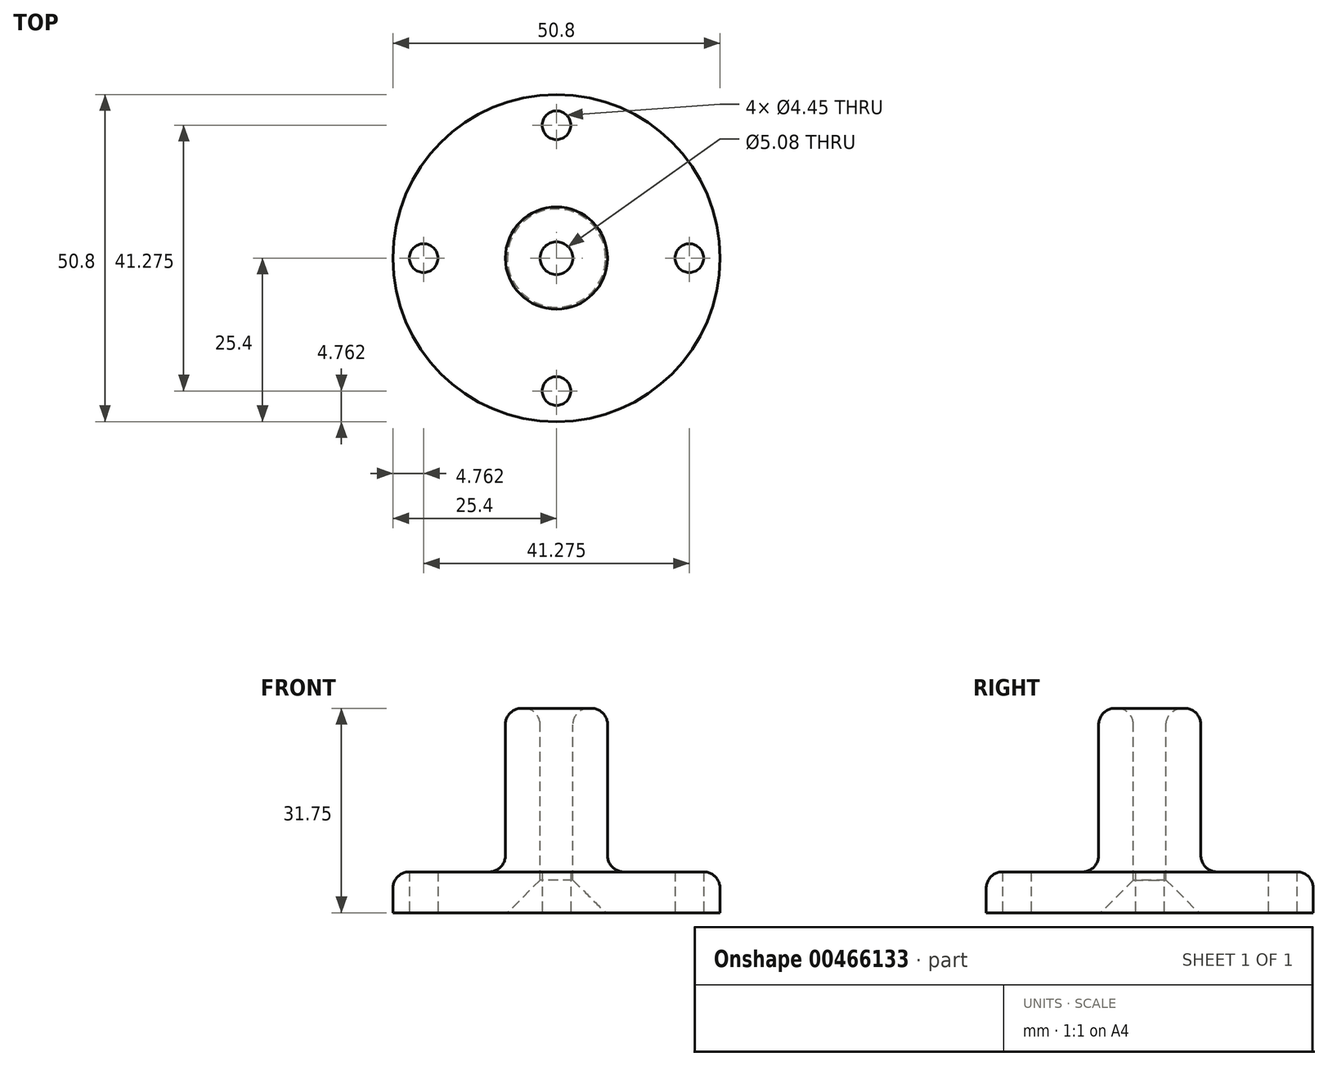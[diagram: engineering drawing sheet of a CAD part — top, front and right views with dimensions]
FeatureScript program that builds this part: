
annotation { "Feature Type Name" : "Feature", "Feature Type Description" : "" }
export const myFeature = defineFeature(function(context is Context, id is Id, definition is map)
    precondition{}
    {
        {
            var Q0;
            Q0=qCreatedBy(makeId("Top.planeOp"),FACE);
            var sketch = newSketch(context, id + "F0", { "sketchPlane" : qUnion([Q0])});
            skCircle(sketch, "E0", {"center": v(0, 0) * mm, "radius": 25.4 * mm});
            skLineSegment(sketch, "E1", {"start": v(0, 41.42) * mm, "end": v(0, -53.18) * mm, "construction": true});
            skLineSegment(sketch, "E2", {"start": v(45.55, 0) * mm, "end": v(-36.4, 0) * mm, "construction": true});
            skCircle(sketch, "E3", {"center": v(0, 0) * mm, "radius": 20.64 * mm, "construction": true});
            skCircle(sketch, "E4", {"center": v(0, 20.64) * mm, "radius": 2.22 * mm});
            skCircle(sketch, "E5.1.0", {"center": v(20.64, 0) * mm, "radius": 2.22 * mm});
            skCircle(sketch, "E5.2.0", {"center": v(0, -20.64) * mm, "radius": 2.22 * mm});
            skCircle(sketch, "E5.3.0", {"center": v(-20.64, 0) * mm, "radius": 2.22 * mm});
            skLineSegment(sketch, "E5.anchor1", {"start": v(0, 0) * mm, "end": v(0, 20.64) * mm, "construction": true});
            skLineSegment(sketch, "E5.anchor2", {"start": v(0, 0) * mm, "end": v(-20.64, 0) * mm, "construction": true});
            skArc(sketch, "E6", {"start": v(-4.06, 0) * mm, "mid": v(0, -4.06) * mm, "end": v(4.06, 0) * mm});
            skArc(sketch, "E7.0", {"start": v(1.4, 10.32) * mm, "mid": v(0.7, 10.4) * mm, "end": v(0, 10.41) * mm});
            skLineSegment(sketch, "E8", {"start": v(0, 10.32) * mm, "end": v(46.94, 10.32) * mm, "construction": true});
            skLineSegment(sketch, "E9", {"start": v(10.41, 0) * mm, "end": v(10.41, 10.32) * mm});
            skLineSegment(sketch, "E10", {"start": v(4.06, 0) * mm, "end": v(4.06, 10.32) * mm});
            skArc(sketch, "E11", {"start": v(10.41, 10.32) * mm, "mid": v(7.24, 14.11) * mm, "end": v(4.06, 10.32) * mm});
            skArc(sketch, "E12.trimOffspring", {"start": v(-10.41, 0) * mm, "mid": v(0, -10.41) * mm, "end": v(10.41, 0) * mm});
            skLineSegment(sketch, "E13.MirrorCS", {"start": v(-4.06, 0) * mm, "end": v(-4.06, 10.32) * mm});
            skArc(sketch, "E14.MirrorCS", {"start": v(-10.41, 10.32) * mm, "mid": v(-7.24, 14.11) * mm, "end": v(-4.06, 10.32) * mm});
            skLineSegment(sketch, "E15.MirrorCS", {"start": v(-10.41, 0) * mm, "end": v(-10.41, 10.32) * mm});
            skSolve(sketch);
        }
        {
            var Q0;
            Q0=makeQuery(id+"F0.imprint","IMPRINT",FACE,{"disambiguationData":[TD([[makeQuery(id+"F0.imprint","IMPRINT",EDGE,{"derivedFrom":sQuery(id+"F0.wireOp",EDGE,"E0")}),1.0]])]});
            var Q1;
            Q1=makeQuery(id+"F0.imprint","IMPRINT",FACE,{"disambiguationData":[TD([[makeQuery(id+"F0.imprint","IMPRINT",EDGE,{"derivedFrom":sQuery(id+"F0.wireOp",EDGE,"E6")}),-1.0]])]});
            var Q2;
            Q2=makeQuery(id+"F0.imprint","IMPRINT",FACE,{"disambiguationData":[TD([[makeQuery(id+"F0.imprint","IMPRINT",EDGE,{"derivedFrom":sQuery(id+"F0.wireOp",EDGE,"E5.2.0")}),1.0]])]});
            var Q3;
            Q3=makeQuery(id+"F0.imprint","IMPRINT",FACE,{"disambiguationData":[TD([[makeQuery(id+"F0.imprint","IMPRINT",EDGE,{"derivedFrom":sQuery(id+"F0.wireOp",EDGE,"E5.3.0")}),1.0]])]});
            var Q4;
            Q4=makeQuery(id+"F0.imprint","IMPRINT",FACE,{"disambiguationData":[TD([[makeQuery(id+"F0.imprint","IMPRINT",EDGE,{"derivedFrom":sQuery(id+"F0.wireOp",EDGE,"E4")}),1.0]])]});
            var Q5;
            Q5=makeQuery(id+"F0.imprint","IMPRINT",FACE,{"disambiguationData":[TD([[makeQuery(id+"F0.imprint","IMPRINT",EDGE,{"derivedFrom":sQuery(id+"F0.wireOp",EDGE,"E5.1.0")}),1.0]])]});
            extrude(context, id + "F1", {"entities" : qUnion([Q0, Q1, Q2, Q3, Q4, Q5]), "depth" : 6.35 * mm});
        }
        {
            var Q0;
            Q0=makeQuery(id+"F1.opExtrude","CAP_FACE",FACE,{"disambiguationData":[OSD([sQuery(id+"F0.wireOp",EDGE,"E0"),sQuery(id+"F0.wireOp",EDGE,"E4"),sQuery(id+"F0.wireOp",EDGE,"E5.1.0"),sQuery(id+"F0.wireOp",EDGE,"E5.2.0"),sQuery(id+"F0.wireOp",EDGE,"E5.3.0")])],"isStart":false});
            var sketch = newSketch(context, id + "F2", { "sketchPlane" : qUnion([Q0])});
            skCircle(sketch, "E16", {"center": v(0, 0) * mm, "radius": 2.54 * mm});
            skCircle(sketch, "E17", {"center": v(0, 0) * mm, "radius": 7.94 * mm});
            skSolve(sketch);
        }
        {
            var Q0;
            Q0=makeQuery(id+"F1.opExtrude","CAP_EDGE",EDGE,{"disambiguationData":[OSD([sQuery(id+"F0.wireOp",EDGE,"E0")])],"isStart":false});
            fillet(context, id + "F3", {"entities" : qUnion([Q0]), "radius" : 2.54 * mm, "tangentPropagation" : true, "allowEdgeOverflow" : false});
        }
        {
            var Q0;
            Q0=makeQuery(id+"F2.imprint","IMPRINT",FACE,{"disambiguationData":[TD([[makeQuery(id+"F2.imprint","IMPRINT",EDGE,{"derivedFrom":sQuery(id+"F2.wireOp",EDGE,"E16")}),1.0]])]});
            extrude(context, id + "F4", {"entities" : qUnion([Q0]), "operationType" : NewBodyOperationType.REMOVE, "oppositeDirection" : true, "depth" : 25.4 * mm});
        }
        {
            var Q0;
            Q0=makeQuery(id+"F2.imprint","IMPRINT",FACE,{"disambiguationData":[TD([[makeQuery(id+"F2.imprint","IMPRINT",EDGE,{"derivedFrom":sQuery(id+"F2.wireOp",EDGE,"E16")}),-1.0]])]});
            extrude(context, id + "F5", {"entities" : qUnion([Q0]), "operationType" : NewBodyOperationType.ADD, "depth" : 25.4 * mm});
        }
        {
            var Q0;
            {var subQ0=sQuery(id+"F0.wireOp",EDGE,"E0");Q0=makeQuery(id+"F5.boolean.opBoolean","SPLIT",FACE,{"disambiguationData":[TD([makeQuery(id+"F3.opFillet","BLEND_FACE",FACE,{"disambiguationData":[OSD([subQ0])]})])],"derivedFrom":makeQuery(id+"F1.opExtrude","CAP_FACE",FACE,{"disambiguationData":[OSD([subQ0])],"isStart":false})});}
            fillet(context, id + "F6", {"entities" : qUnion([Q0]), "radius" : 2.54 * mm, "tangentPropagation" : true, "allowEdgeOverflow" : false});
        }
        {
            var Q0;
            Q0=makeQuery(id+"F0.imprint","IMPRINT",FACE,{"disambiguationData":[TD([[makeQuery(id+"F0.imprint","IMPRINT",EDGE,{"derivedFrom":sQuery(id+"F0.wireOp",EDGE,"E5.1.0")}),1.0]])]});
            var Q1;
            Q1=makeQuery(id+"F0.imprint","IMPRINT",FACE,{"disambiguationData":[TD([[makeQuery(id+"F0.imprint","IMPRINT",EDGE,{"derivedFrom":sQuery(id+"F0.wireOp",EDGE,"E4")}),1.0]])]});
            var Q2;
            Q2=makeQuery(id+"F0.imprint","IMPRINT",FACE,{"disambiguationData":[TD([[makeQuery(id+"F0.imprint","IMPRINT",EDGE,{"derivedFrom":sQuery(id+"F0.wireOp",EDGE,"E5.3.0")}),1.0]])]});
            var Q3;
            Q3=makeQuery(id+"F0.imprint","IMPRINT",FACE,{"disambiguationData":[TD([[makeQuery(id+"F0.imprint","IMPRINT",EDGE,{"derivedFrom":sQuery(id+"F0.wireOp",EDGE,"E5.2.0")}),1.0]])]});
            extrude(context, id + "F7", {"entities" : qUnion([Q0, Q1, Q2, Q3]), "operationType" : NewBodyOperationType.REMOVE, "depth" : 25.4 * mm});
        }
        {
            var Q0;
            Q0=makeQuery(id+"F5.opExtrude","CAP_FACE",FACE,{"disambiguationData":[OSD([sQuery(id+"F2.wireOp",EDGE,"E16"),sQuery(id+"F2.wireOp",EDGE,"E17")])],"isStart":false});
            fillet(context, id + "F8", {"entities" : qUnion([Q0]), "radius" : 2.54 * mm, "tangentPropagation" : true, "allowEdgeOverflow" : false});
        }
        {
            var Q0;
            Q0=makeQuery(id+"F4.boolean.opBoolean","INTERSECT",EDGE,{"derivedFrom":[makeQuery(id+"F1.opExtrude","CAP_FACE",FACE,{"disambiguationData":[OSD([sQuery(id+"F0.wireOp",EDGE,"E0")])],"isStart":true}),makeQuery(id+"F4.opExtrude","SWEPT_FACE",FACE,{"disambiguationData":[OSD([sQuery(id+"F2.wireOp",EDGE,"E16")])]})]});
            chamfer(context, id + "F9", {"entities" : qUnion([Q0]), "width" : 5.08 * mm, "tangentPropagation" : true});
        }
    });
